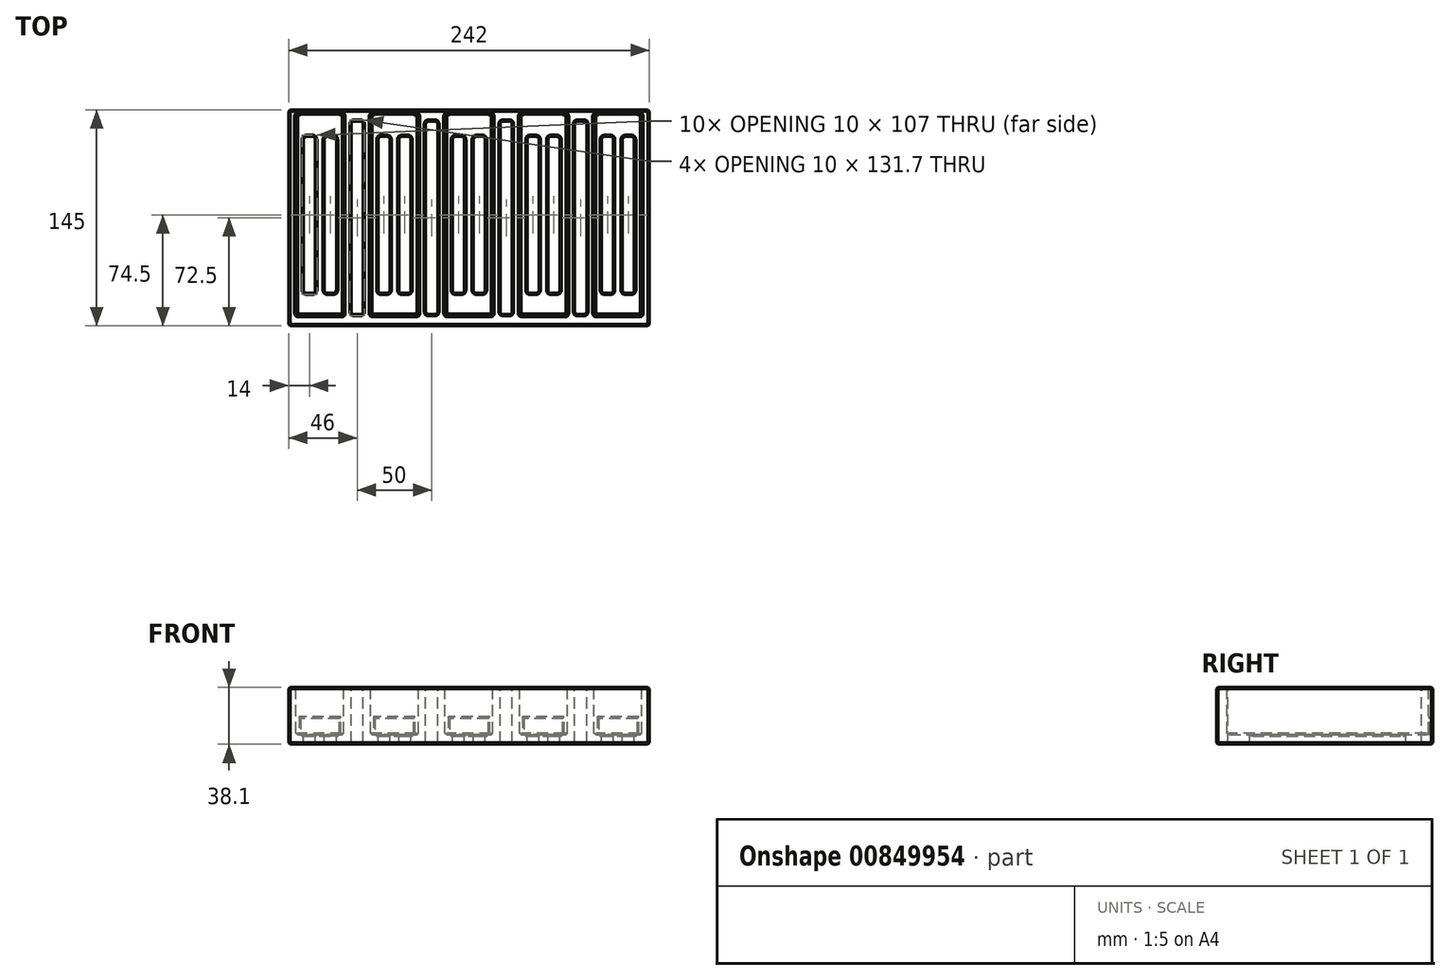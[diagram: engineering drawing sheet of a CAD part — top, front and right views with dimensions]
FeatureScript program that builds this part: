
annotation { "Feature Type Name" : "Feature", "Feature Type Description" : "" }
export const myFeature = defineFeature(function(context is Context, id is Id, definition is map)
    precondition{}
    {
        {
            var Q0;
            Q0=qCreatedBy(makeId("Top.planeOp"),FACE);
            var sketch = newSketch(context, id + "F0", { "sketchPlane" : qUnion([Q0])});
            skLineSegment(sketch, "E0.bottom", {"start": v(121, -72.5) * mm, "end": v(-121, -72.5) * mm});
            skLineSegment(sketch, "E0.top", {"start": v(121, 72.5) * mm, "end": v(-121, 72.5) * mm});
            skLineSegment(sketch, "E0.left", {"start": v(121, -72.5) * mm, "end": v(121, 72.5) * mm});
            skLineSegment(sketch, "E0.right", {"start": v(-121, -72.5) * mm, "end": v(-121, 72.5) * mm});
            skPoint(sketch, "E0.middle", {"position": v(0, 0) * mm});
            skSolve(sketch);
        }
        {
            var Q0;
            Q0=makeQuery(id+"F0.imprint","IMPRINT",FACE,{"disambiguationData":[TD([[makeQuery(id+"F0.imprint","IMPRINT",EDGE,{"derivedFrom":sQuery(id+"F0.wireOp",EDGE,"E0.bottom")}),-1.0]])]});
            extrude(context, id + "F1", {"entities" : qUnion([Q0]), "depth" : 38.1 * mm, "offsetDistance" : 25.4 * mm});
        }
        {
            var Q0;
            Q0=makeQuery(id+"F1.opExtrude","CAP_FACE",FACE,{"disambiguationData":[OSD([sQuery(id+"F0.wireOp",EDGE,"E0.bottom"),sQuery(id+"F0.wireOp",EDGE,"E0.top"),sQuery(id+"F0.wireOp",EDGE,"E0.left"),sQuery(id+"F0.wireOp",EDGE,"E0.right")])],"isStart":false});
            var sketch = newSketch(context, id + "F2", { "sketchPlane" : qUnion([Q0])});
            skLineSegment(sketch, "E1.bottom", {"start": v(-116, 69.5) * mm, "end": v(-84, 69.5) * mm});
            skLineSegment(sketch, "E1.top", {"start": v(-116, -65.5) * mm, "end": v(-84, -65.5) * mm});
            skLineSegment(sketch, "E1.left", {"start": v(-116, 69.5) * mm, "end": v(-116, -65.5) * mm});
            skLineSegment(sketch, "E1.right", {"start": v(-84, 69.5) * mm, "end": v(-84, -65.5) * mm});
            skLineSegment(sketch, "E2.1.0.0", {"start": v(-34, 69.5) * mm, "end": v(-34, -65.5) * mm});
            skLineSegment(sketch, "E2.1.0.1", {"start": v(-66, 69.5) * mm, "end": v(-34, 69.5) * mm});
            skLineSegment(sketch, "E2.1.0.2", {"start": v(-66, 69.5) * mm, "end": v(-66, -65.5) * mm});
            skLineSegment(sketch, "E2.1.0.3", {"start": v(-66, -65.5) * mm, "end": v(-34, -65.5) * mm});
            skLineSegment(sketch, "E2.2.0.0", {"start": v(16, 69.5) * mm, "end": v(16, -65.5) * mm});
            skLineSegment(sketch, "E2.2.0.1", {"start": v(-16, 69.5) * mm, "end": v(16, 69.5) * mm});
            skLineSegment(sketch, "E2.2.0.2", {"start": v(-16, 69.5) * mm, "end": v(-16, -65.5) * mm});
            skLineSegment(sketch, "E2.2.0.3", {"start": v(-16, -65.5) * mm, "end": v(16, -65.5) * mm});
            skLineSegment(sketch, "E2.direction1", {"start": v(-116, -65.5) * mm, "end": v(-66, -65.5) * mm, "construction": true});
            skLineSegment(sketch, "E3.0.3.0", {"start": v(66, 69.5) * mm, "end": v(66, -65.5) * mm});
            skLineSegment(sketch, "E3.3.3.0", {"start": v(34, 69.5) * mm, "end": v(66, 69.5) * mm});
            skLineSegment(sketch, "E3.6.3.0", {"start": v(34, 69.5) * mm, "end": v(34, -65.5) * mm});
            skLineSegment(sketch, "E3.9.3.0", {"start": v(34, -65.5) * mm, "end": v(66, -65.5) * mm});
            skLineSegment(sketch, "E3.0.4.0", {"start": v(116, 69.5) * mm, "end": v(116, -65.5) * mm});
            skLineSegment(sketch, "E3.3.4.0", {"start": v(84, 69.5) * mm, "end": v(116, 69.5) * mm});
            skLineSegment(sketch, "E3.6.4.0", {"start": v(84, 69.5) * mm, "end": v(84, -65.5) * mm});
            skLineSegment(sketch, "E3.9.4.0", {"start": v(84, -65.5) * mm, "end": v(116, -65.5) * mm});
            skSolve(sketch);
        }
        {
            var Q0;
            Q0 = qSketchRegion(id + "F2", true);
            extrude(context, id + "F3", {"entities" : qUnion([Q0]), "operationType" : NewBodyOperationType.REMOVE, "oppositeDirection" : true, "depth" : 31.75 * mm, "offsetDistance" : 25.4 * mm});
        }
        {
            var Q0;
            Q0=makeQuery(id+"F1.opExtrude","SWEPT_FACE",FACE,{"disambiguationData":[OSD([sQuery(id+"F0.wireOp",EDGE,"E0.top")])]});
            var sketch = newSketch(context, id + "F4", { "sketchPlane" : qUnion([Q0])});
            skLineSegment(sketch, "E4.top", {"start": v(87, 6.35) * mm, "end": v(113, 6.35) * mm});
            skLineSegment(sketch, "E4.left", {"start": v(87, 17.35) * mm, "end": v(87, 6.35) * mm});
            skLineSegment(sketch, "E4.right", {"start": v(113, 17.35) * mm, "end": v(113, 6.35) * mm});
            skLineSegment(sketch, "E5.1.0.1", {"start": v(37, 17.35) * mm, "end": v(37, 6.35) * mm});
            skLineSegment(sketch, "E5.1.0.2", {"start": v(37, 6.35) * mm, "end": v(63, 6.35) * mm});
            skLineSegment(sketch, "E5.1.0.3", {"start": v(63, 17.35) * mm, "end": v(63, 6.35) * mm});
            skLineSegment(sketch, "E5.2.0.1", {"start": v(-13, 17.35) * mm, "end": v(-13, 6.35) * mm});
            skLineSegment(sketch, "E5.2.0.2", {"start": v(-13, 6.35) * mm, "end": v(13, 6.35) * mm});
            skLineSegment(sketch, "E5.2.0.3", {"start": v(13, 17.35) * mm, "end": v(13, 6.35) * mm});
            skLineSegment(sketch, "E5.3.0.1", {"start": v(-63, 17.35) * mm, "end": v(-63, 6.35) * mm});
            skLineSegment(sketch, "E5.3.0.2", {"start": v(-63, 6.35) * mm, "end": v(-37, 6.35) * mm});
            skLineSegment(sketch, "E5.3.0.3", {"start": v(-37, 17.35) * mm, "end": v(-37, 6.35) * mm});
            skLineSegment(sketch, "E5.4.0.1", {"start": v(-113, 17.35) * mm, "end": v(-113, 6.35) * mm});
            skLineSegment(sketch, "E5.4.0.2", {"start": v(-113, 6.35) * mm, "end": v(-87, 6.35) * mm});
            skLineSegment(sketch, "E5.4.0.3", {"start": v(-87, 17.35) * mm, "end": v(-87, 6.35) * mm});
            skLineSegment(sketch, "E5.direction1", {"start": v(87, 17.35) * mm, "end": v(37, 17.35) * mm, "construction": true});
            skLineSegment(sketch, "E6", {"start": v(87, 17.35) * mm, "end": v(113, 17.35) * mm});
            skLineSegment(sketch, "E7.1.0.0", {"start": v(37, 17.35) * mm, "end": v(63, 17.35) * mm});
            skLineSegment(sketch, "E7.2.0.0", {"start": v(-13, 17.35) * mm, "end": v(13, 17.35) * mm});
            skLineSegment(sketch, "E7.3.0.0", {"start": v(-63, 17.35) * mm, "end": v(-37, 17.35) * mm});
            skLineSegment(sketch, "E7.4.0.0", {"start": v(-113, 17.35) * mm, "end": v(-87, 17.35) * mm});
            skSolve(sketch);
        }
        {
            var Q0;
            Q0=makeQuery(id+"F4.imprint","IMPRINT",FACE,{"disambiguationData":[TD([[makeQuery(id+"F4.imprint","IMPRINT",EDGE,{"derivedFrom":sQuery(id+"F4.wireOp",EDGE,"E4.top")}),1.0]])]});
            var Q1;
            Q1=makeQuery(id+"F4.imprint","IMPRINT",FACE,{"disambiguationData":[TD([[makeQuery(id+"F4.imprint","IMPRINT",EDGE,{"derivedFrom":sQuery(id+"F4.wireOp",EDGE,"E5.1.0.1")}),1.0]])]});
            var Q2;
            Q2=makeQuery(id+"F4.imprint","IMPRINT",FACE,{"disambiguationData":[TD([[makeQuery(id+"F4.imprint","IMPRINT",EDGE,{"derivedFrom":sQuery(id+"F4.wireOp",EDGE,"E5.2.0.1")}),1.0]])]});
            var Q3;
            Q3=makeQuery(id+"F4.imprint","IMPRINT",FACE,{"disambiguationData":[TD([[makeQuery(id+"F4.imprint","IMPRINT",EDGE,{"derivedFrom":sQuery(id+"F4.wireOp",EDGE,"E5.3.0.1")}),1.0]])]});
            var Q4;
            Q4=makeQuery(id+"F4.imprint","IMPRINT",FACE,{"disambiguationData":[TD([[makeQuery(id+"F4.imprint","IMPRINT",EDGE,{"derivedFrom":sQuery(id+"F4.wireOp",EDGE,"E5.4.0.1")}),1.0]])]});
            extrude(context, id + "F5", {"entities" : qUnion([Q0, Q1, Q2, Q3, Q4]), "operationType" : NewBodyOperationType.REMOVE, "endBound" : BoundingType.UP_TO_NEXT, "oppositeDirection" : true, "depth" : 25.4 * mm, "offsetDistance" : 25.4 * mm});
        }
        {
            var Q0;
            Q0=makeQuery(id+"F1.opExtrude","CAP_FACE",FACE,{"disambiguationData":[OSD([sQuery(id+"F0.wireOp",EDGE,"E0.bottom"),sQuery(id+"F0.wireOp",EDGE,"E0.top"),sQuery(id+"F0.wireOp",EDGE,"E0.left"),sQuery(id+"F0.wireOp",EDGE,"E0.right")])],"isStart":false});
            var sketch = newSketch(context, id + "F6", { "sketchPlane" : qUnion([Q0])});
            skLineSegment(sketch, "E8.bottom", {"start": v(-77, 64.85) * mm, "end": v(-73, 64.85) * mm});
            skLineSegment(sketch, "E8.top", {"start": v(-77, -64.85) * mm, "end": v(-73, -64.85) * mm});
            skLineSegment(sketch, "E8.left", {"start": v(-79, 62.85) * mm, "end": v(-79, -62.85) * mm});
            skLineSegment(sketch, "E8.right", {"start": v(-71, 62.85) * mm, "end": v(-71, -62.85) * mm});
            skPoint(sketch, "E9.visualSharp", {"position": v(-79, 64.85) * mm});
            skArc(sketch, "E9.filletArc", {"start": v(-77, 64.85) * mm, "mid": v(-78.41, 64.26) * mm, "end": v(-79, 62.85) * mm});
            skPoint(sketch, "E10.visualSharp", {"position": v(-71, 64.85) * mm});
            skArc(sketch, "E10.filletArc", {"start": v(-71, 62.85) * mm, "mid": v(-71.59, 64.26) * mm, "end": v(-73, 64.85) * mm});
            skPoint(sketch, "E11.visualSharp", {"position": v(-79, -64.85) * mm});
            skArc(sketch, "E11.filletArc", {"start": v(-79, -62.85) * mm, "mid": v(-78.41, -64.26) * mm, "end": v(-77, -64.85) * mm});
            skPoint(sketch, "E12.visualSharp", {"position": v(-71, -64.85) * mm});
            skArc(sketch, "E12.filletArc", {"start": v(-73, -64.85) * mm, "mid": v(-71.59, -64.26) * mm, "end": v(-71, -62.85) * mm});
            skLineSegment(sketch, "E13.1.0.0", {"start": v(-29, 62.85) * mm, "end": v(-29, -62.85) * mm});
            skLineSegment(sketch, "E13.1.0.1", {"start": v(-21, 62.85) * mm, "end": v(-21, -62.85) * mm});
            skArc(sketch, "E13.1.0.2", {"start": v(-29, -62.85) * mm, "mid": v(-28.41, -64.26) * mm, "end": v(-27, -64.85) * mm});
            skLineSegment(sketch, "E13.1.0.3", {"start": v(-27, -64.85) * mm, "end": v(-23, -64.85) * mm});
            skArc(sketch, "E13.1.0.4", {"start": v(-23, -64.85) * mm, "mid": v(-21.59, -64.26) * mm, "end": v(-21, -62.85) * mm});
            skArc(sketch, "E13.1.0.5", {"start": v(-27, 64.85) * mm, "mid": v(-28.41, 64.26) * mm, "end": v(-29, 62.85) * mm});
            skLineSegment(sketch, "E13.1.0.6", {"start": v(-27, 64.85) * mm, "end": v(-23, 64.85) * mm});
            skArc(sketch, "E13.1.0.7", {"start": v(-21, 62.85) * mm, "mid": v(-21.59, 64.26) * mm, "end": v(-23, 64.85) * mm});
            skLineSegment(sketch, "E13.2.0.0", {"start": v(21, 62.85) * mm, "end": v(21, -62.85) * mm});
            skLineSegment(sketch, "E13.2.0.1", {"start": v(29, 62.85) * mm, "end": v(29, -62.85) * mm});
            skArc(sketch, "E13.2.0.2", {"start": v(21, -62.85) * mm, "mid": v(21.59, -64.26) * mm, "end": v(23, -64.85) * mm});
            skLineSegment(sketch, "E13.2.0.3", {"start": v(23, -64.85) * mm, "end": v(27, -64.85) * mm});
            skArc(sketch, "E13.2.0.4", {"start": v(27, -64.85) * mm, "mid": v(28.41, -64.26) * mm, "end": v(29, -62.85) * mm});
            skArc(sketch, "E13.2.0.5", {"start": v(23, 64.85) * mm, "mid": v(21.59, 64.26) * mm, "end": v(21, 62.85) * mm});
            skLineSegment(sketch, "E13.2.0.6", {"start": v(23, 64.85) * mm, "end": v(27, 64.85) * mm});
            skArc(sketch, "E13.2.0.7", {"start": v(29, 62.85) * mm, "mid": v(28.41, 64.26) * mm, "end": v(27, 64.85) * mm});
            skLineSegment(sketch, "E13.3.0.0", {"start": v(71, 62.85) * mm, "end": v(71, -62.85) * mm});
            skLineSegment(sketch, "E13.3.0.1", {"start": v(79, 62.85) * mm, "end": v(79, -62.85) * mm});
            skArc(sketch, "E13.3.0.2", {"start": v(71, -62.85) * mm, "mid": v(71.59, -64.26) * mm, "end": v(73, -64.85) * mm});
            skLineSegment(sketch, "E13.3.0.3", {"start": v(73, -64.85) * mm, "end": v(77, -64.85) * mm});
            skArc(sketch, "E13.3.0.4", {"start": v(77, -64.85) * mm, "mid": v(78.41, -64.26) * mm, "end": v(79, -62.85) * mm});
            skArc(sketch, "E13.3.0.5", {"start": v(73, 64.85) * mm, "mid": v(71.59, 64.26) * mm, "end": v(71, 62.85) * mm});
            skLineSegment(sketch, "E13.3.0.6", {"start": v(73, 64.85) * mm, "end": v(77, 64.85) * mm});
            skArc(sketch, "E13.3.0.7", {"start": v(79, 62.85) * mm, "mid": v(78.41, 64.26) * mm, "end": v(77, 64.85) * mm});
            skLineSegment(sketch, "E13.direction1", {"start": v(-79, -62.85) * mm, "end": v(-29, -62.85) * mm, "construction": true});
            skSolve(sketch);
        }
        {
            var Q0;
            Q0=makeQuery(id+"F6.imprint","IMPRINT",FACE,{"disambiguationData":[TD([[makeQuery(id+"F6.imprint","IMPRINT",EDGE,{"derivedFrom":sQuery(id+"F6.wireOp",EDGE,"E8.bottom")}),-1.0]])]});
            var Q1;
            Q1=makeQuery(id+"F6.imprint","IMPRINT",FACE,{"disambiguationData":[TD([[makeQuery(id+"F6.imprint","IMPRINT",EDGE,{"derivedFrom":sQuery(id+"F6.wireOp",EDGE,"E13.2.0.0")}),1.0]])]});
            var Q2;
            Q2=makeQuery(id+"F6.imprint","IMPRINT",FACE,{"disambiguationData":[TD([[makeQuery(id+"F6.imprint","IMPRINT",EDGE,{"derivedFrom":sQuery(id+"F6.wireOp",EDGE,"E13.3.0.0")}),1.0]])]});
            var Q3;
            Q3=makeQuery(id+"F6.imprint","IMPRINT",FACE,{"disambiguationData":[TD([[makeQuery(id+"F6.imprint","IMPRINT",EDGE,{"derivedFrom":sQuery(id+"F6.wireOp",EDGE,"E13.1.0.0")}),1.0]])]});
            extrude(context, id + "F7", {"entities" : qUnion([Q0, Q1, Q2, Q3]), "operationType" : NewBodyOperationType.REMOVE, "endBound" : BoundingType.THROUGH_ALL, "oppositeDirection" : true, "depth" : 25 * mm, "offsetDistance" : 25 * mm});
        }
        {
            var Q0;
            Q0=makeQuery(id+"F3.boolean.opBoolean","COPY",EDGE,{"derivedFrom":makeQuery(id+"F3.opExtrude","SWEPT_EDGE",EDGE,{"disambiguationData":[OSD([sQuery(id+"F2.wireOp",EDGE,"E1.bottom"),sQuery(id+"F2.wireOp",EDGE,"E1.left")])]})});
            var Q1;
            Q1=makeQuery(id+"F3.boolean.opBoolean","COPY",EDGE,{"derivedFrom":makeQuery(id+"F3.opExtrude","SWEPT_EDGE",EDGE,{"disambiguationData":[OSD([sQuery(id+"F2.wireOp",EDGE,"E1.bottom"),sQuery(id+"F2.wireOp",EDGE,"E1.right")])]})});
            var Q2;
            Q2=makeQuery(id+"F3.boolean.opBoolean","COPY",EDGE,{"derivedFrom":makeQuery(id+"F3.opExtrude","SWEPT_EDGE",EDGE,{"disambiguationData":[OSD([sQuery(id+"F2.wireOp",EDGE,"E1.top"),sQuery(id+"F2.wireOp",EDGE,"E1.left")])]})});
            var Q3;
            Q3=makeQuery(id+"F3.boolean.opBoolean","COPY",EDGE,{"derivedFrom":makeQuery(id+"F3.opExtrude","SWEPT_EDGE",EDGE,{"disambiguationData":[OSD([sQuery(id+"F2.wireOp",EDGE,"E1.top"),sQuery(id+"F2.wireOp",EDGE,"E1.right")])]})});
            var Q4;
            Q4=makeQuery(id+"F3.boolean.opBoolean","COPY",EDGE,{"derivedFrom":makeQuery(id+"F3.opExtrude","SWEPT_EDGE",EDGE,{"disambiguationData":[OSD([sQuery(id+"F2.wireOp",EDGE,"E2.1.0.2"),sQuery(id+"F2.wireOp",EDGE,"E2.1.0.3")])]})});
            var Q5;
            Q5=makeQuery(id+"F3.boolean.opBoolean","COPY",EDGE,{"derivedFrom":makeQuery(id+"F3.opExtrude","SWEPT_EDGE",EDGE,{"disambiguationData":[OSD([sQuery(id+"F2.wireOp",EDGE,"E2.1.0.1"),sQuery(id+"F2.wireOp",EDGE,"E2.1.0.2")])]})});
            var Q6;
            Q6=makeQuery(id+"F3.boolean.opBoolean","COPY",EDGE,{"derivedFrom":makeQuery(id+"F3.opExtrude","SWEPT_EDGE",EDGE,{"disambiguationData":[OSD([sQuery(id+"F2.wireOp",EDGE,"E2.1.0.0"),sQuery(id+"F2.wireOp",EDGE,"E2.1.0.1")])]})});
            var Q7;
            Q7=makeQuery(id+"F3.boolean.opBoolean","COPY",EDGE,{"derivedFrom":makeQuery(id+"F3.opExtrude","SWEPT_EDGE",EDGE,{"disambiguationData":[OSD([sQuery(id+"F2.wireOp",EDGE,"E2.1.0.0"),sQuery(id+"F2.wireOp",EDGE,"E2.1.0.3")])]})});
            var Q8;
            Q8=makeQuery(id+"F3.boolean.opBoolean","COPY",EDGE,{"derivedFrom":makeQuery(id+"F3.opExtrude","SWEPT_EDGE",EDGE,{"disambiguationData":[OSD([sQuery(id+"F2.wireOp",EDGE,"E2.2.0.1"),sQuery(id+"F2.wireOp",EDGE,"E2.2.0.2")])]})});
            var Q9;
            Q9=makeQuery(id+"F3.boolean.opBoolean","COPY",EDGE,{"derivedFrom":makeQuery(id+"F3.opExtrude","SWEPT_EDGE",EDGE,{"disambiguationData":[OSD([sQuery(id+"F2.wireOp",EDGE,"E2.2.0.0"),sQuery(id+"F2.wireOp",EDGE,"E2.2.0.1")])]})});
            var Q10;
            Q10=makeQuery(id+"F3.boolean.opBoolean","COPY",EDGE,{"derivedFrom":makeQuery(id+"F3.opExtrude","SWEPT_EDGE",EDGE,{"disambiguationData":[OSD([sQuery(id+"F2.wireOp",EDGE,"E2.2.0.2"),sQuery(id+"F2.wireOp",EDGE,"E2.2.0.3")])]})});
            var Q11;
            Q11=makeQuery(id+"F3.boolean.opBoolean","COPY",EDGE,{"derivedFrom":makeQuery(id+"F3.opExtrude","SWEPT_EDGE",EDGE,{"disambiguationData":[OSD([sQuery(id+"F2.wireOp",EDGE,"E2.2.0.0"),sQuery(id+"F2.wireOp",EDGE,"E2.2.0.3")])]})});
            var Q12;
            Q12=makeQuery(id+"F3.boolean.opBoolean","COPY",EDGE,{"derivedFrom":makeQuery(id+"F3.opExtrude","SWEPT_EDGE",EDGE,{"disambiguationData":[OSD([sQuery(id+"F2.wireOp",EDGE,"E3.3.3.0"),sQuery(id+"F2.wireOp",EDGE,"E3.6.3.0")])]})});
            var Q13;
            Q13=makeQuery(id+"F3.boolean.opBoolean","COPY",EDGE,{"derivedFrom":makeQuery(id+"F3.opExtrude","SWEPT_EDGE",EDGE,{"disambiguationData":[OSD([sQuery(id+"F2.wireOp",EDGE,"E3.6.3.0"),sQuery(id+"F2.wireOp",EDGE,"E3.9.3.0")])]})});
            var Q14;
            Q14=makeQuery(id+"F3.boolean.opBoolean","COPY",EDGE,{"derivedFrom":makeQuery(id+"F3.opExtrude","SWEPT_EDGE",EDGE,{"disambiguationData":[OSD([sQuery(id+"F2.wireOp",EDGE,"E3.0.3.0"),sQuery(id+"F2.wireOp",EDGE,"E3.9.3.0")])]})});
            var Q15;
            Q15=makeQuery(id+"F3.boolean.opBoolean","COPY",EDGE,{"derivedFrom":makeQuery(id+"F3.opExtrude","SWEPT_EDGE",EDGE,{"disambiguationData":[OSD([sQuery(id+"F2.wireOp",EDGE,"E3.0.3.0"),sQuery(id+"F2.wireOp",EDGE,"E3.3.3.0")])]})});
            var Q16;
            Q16=makeQuery(id+"F3.boolean.opBoolean","COPY",EDGE,{"derivedFrom":makeQuery(id+"F3.opExtrude","SWEPT_EDGE",EDGE,{"disambiguationData":[OSD([sQuery(id+"F2.wireOp",EDGE,"E3.3.4.0"),sQuery(id+"F2.wireOp",EDGE,"E3.6.4.0")])]})});
            var Q17;
            Q17=makeQuery(id+"F3.boolean.opBoolean","COPY",EDGE,{"derivedFrom":makeQuery(id+"F3.opExtrude","SWEPT_EDGE",EDGE,{"disambiguationData":[OSD([sQuery(id+"F2.wireOp",EDGE,"E3.0.4.0"),sQuery(id+"F2.wireOp",EDGE,"E3.3.4.0")])]})});
            var Q18;
            Q18=makeQuery(id+"F3.boolean.opBoolean","COPY",EDGE,{"derivedFrom":makeQuery(id+"F3.opExtrude","SWEPT_EDGE",EDGE,{"disambiguationData":[OSD([sQuery(id+"F2.wireOp",EDGE,"E3.6.4.0"),sQuery(id+"F2.wireOp",EDGE,"E3.9.4.0")])]})});
            var Q19;
            Q19=makeQuery(id+"F3.boolean.opBoolean","COPY",EDGE,{"derivedFrom":makeQuery(id+"F3.opExtrude","SWEPT_EDGE",EDGE,{"disambiguationData":[OSD([sQuery(id+"F2.wireOp",EDGE,"E3.0.4.0"),sQuery(id+"F2.wireOp",EDGE,"E3.9.4.0")])]})});
            fillet(context, id + "F8", {"entities" : qUnion([Q0, Q1, Q2, Q3, Q4, Q5, Q6, Q7, Q8, Q9, Q10, Q11, Q12, Q13, Q14, Q15, Q16, Q17, Q18, Q19]), "radius" : 1.5 * mm, "tangentPropagation" : true, "allowEdgeOverflow" : false});
        }
        {
            var Q0;
            Q0=makeQuery(id+"F5.boolean.opBoolean","MERGE",FACE,{"derivedFrom":[makeQuery(id+"F3.boolean.opBoolean","COPY",FACE,{"derivedFrom":makeQuery(id+"F3.opExtrude","CAP_FACE",FACE,{"disambiguationData":[OSD([sQuery(id+"F2.wireOp",EDGE,"E1.bottom"),sQuery(id+"F2.wireOp",EDGE,"E1.top"),sQuery(id+"F2.wireOp",EDGE,"E1.left"),sQuery(id+"F2.wireOp",EDGE,"E1.right")])],"isStart":false})}),makeQuery(id+"F5.opExtrude","SWEPT_FACE",FACE,{"disambiguationData":[OSD([sQuery(id+"F4.wireOp",EDGE,"E4.top")])]})]});
            var sketch = newSketch(context, id + "F9", { "sketchPlane" : qUnion([Q0])});
            skLineSegment(sketch, "E14.bottom", {"start": v(-109, 54.5) * mm, "end": v(-105, 54.5) * mm});
            skLineSegment(sketch, "E14.top", {"start": v(-109, -50.5) * mm, "end": v(-105, -50.5) * mm});
            skLineSegment(sketch, "E14.left", {"start": v(-111, 52.5) * mm, "end": v(-111, -48.5) * mm});
            skLineSegment(sketch, "E14.right", {"start": v(-103, 52.5) * mm, "end": v(-103, -48.5) * mm});
            skLineSegment(sketch, "E15.bottom", {"start": v(-95, 54.5) * mm, "end": v(-91, 54.5) * mm});
            skLineSegment(sketch, "E15.top", {"start": v(-95, -50.5) * mm, "end": v(-91, -50.5) * mm});
            skLineSegment(sketch, "E15.left", {"start": v(-97, 52.5) * mm, "end": v(-97, -48.5) * mm});
            skLineSegment(sketch, "E15.right", {"start": v(-89, 52.5) * mm, "end": v(-89, -48.5) * mm});
            skPoint(sketch, "E16.visualSharp", {"position": v(-111, 54.5) * mm});
            skArc(sketch, "E16.filletArc", {"start": v(-109, 54.5) * mm, "mid": v(-110.41, 53.91) * mm, "end": v(-111, 52.5) * mm});
            skPoint(sketch, "E17.visualSharp", {"position": v(-103, 54.5) * mm});
            skArc(sketch, "E17.filletArc", {"start": v(-103, 52.5) * mm, "mid": v(-103.59, 53.91) * mm, "end": v(-105, 54.5) * mm});
            skPoint(sketch, "E18.visualSharp", {"position": v(-111, -50.5) * mm});
            skArc(sketch, "E18.filletArc", {"start": v(-111, -48.5) * mm, "mid": v(-110.41, -49.91) * mm, "end": v(-109, -50.5) * mm});
            skPoint(sketch, "E19.visualSharp", {"position": v(-103, -50.5) * mm});
            skArc(sketch, "E19.filletArc", {"start": v(-105, -50.5) * mm, "mid": v(-103.59, -49.91) * mm, "end": v(-103, -48.5) * mm});
            skPoint(sketch, "E20.visualSharp", {"position": v(-97, 54.5) * mm});
            skArc(sketch, "E20.filletArc", {"start": v(-95, 54.5) * mm, "mid": v(-96.41, 53.91) * mm, "end": v(-97, 52.5) * mm});
            skPoint(sketch, "E21.visualSharp", {"position": v(-89, 54.5) * mm});
            skArc(sketch, "E21.filletArc", {"start": v(-89, 52.5) * mm, "mid": v(-89.59, 53.91) * mm, "end": v(-91, 54.5) * mm});
            skPoint(sketch, "E22.visualSharp", {"position": v(-89, -50.5) * mm});
            skArc(sketch, "E22.filletArc", {"start": v(-91, -50.5) * mm, "mid": v(-89.59, -49.91) * mm, "end": v(-89, -48.5) * mm});
            skPoint(sketch, "E23.visualSharp", {"position": v(-97, -50.5) * mm});
            skArc(sketch, "E23.filletArc", {"start": v(-97, -48.5) * mm, "mid": v(-96.41, -49.91) * mm, "end": v(-95, -50.5) * mm});
            skLineSegment(sketch, "E24.1.0.0", {"start": v(-47, 52.5) * mm, "end": v(-47, -48.5) * mm});
            skPoint(sketch, "E24.1.0.1", {"position": v(-61, 54.5) * mm});
            skPoint(sketch, "E24.1.0.2", {"position": v(-53, -50.5) * mm});
            skLineSegment(sketch, "E24.1.0.3", {"start": v(-53, 52.5) * mm, "end": v(-53, -48.5) * mm});
            skPoint(sketch, "E24.1.0.4", {"position": v(-61, -50.5) * mm});
            skLineSegment(sketch, "E24.1.0.5", {"start": v(-61, 52.5) * mm, "end": v(-61, -48.5) * mm});
            skPoint(sketch, "E24.1.0.6", {"position": v(-47, -50.5) * mm});
            skPoint(sketch, "E24.1.0.7", {"position": v(-39, 54.5) * mm});
            skPoint(sketch, "E24.1.0.8", {"position": v(-53, 54.5) * mm});
            skLineSegment(sketch, "E24.1.0.9", {"start": v(-39, 52.5) * mm, "end": v(-39, -48.5) * mm});
            skPoint(sketch, "E24.1.0.10", {"position": v(-39, -50.5) * mm});
            skPoint(sketch, "E24.1.0.11", {"position": v(-47, 54.5) * mm});
            skArc(sketch, "E24.1.0.12", {"start": v(-61, -48.5) * mm, "mid": v(-60.41, -49.91) * mm, "end": v(-59, -50.5) * mm});
            skArc(sketch, "E24.1.0.13", {"start": v(-47, -48.5) * mm, "mid": v(-46.41, -49.91) * mm, "end": v(-45, -50.5) * mm});
            skArc(sketch, "E24.1.0.14", {"start": v(-59, 54.5) * mm, "mid": v(-60.41, 53.91) * mm, "end": v(-61, 52.5) * mm});
            skLineSegment(sketch, "E24.1.0.15", {"start": v(-59, -50.5) * mm, "end": v(-55, -50.5) * mm});
            skLineSegment(sketch, "E24.1.0.16", {"start": v(-45, -50.5) * mm, "end": v(-41, -50.5) * mm});
            skArc(sketch, "E24.1.0.17", {"start": v(-45, 54.5) * mm, "mid": v(-46.41, 53.91) * mm, "end": v(-47, 52.5) * mm});
            skArc(sketch, "E24.1.0.18", {"start": v(-55, -50.5) * mm, "mid": v(-53.59, -49.91) * mm, "end": v(-53, -48.5) * mm});
            skArc(sketch, "E24.1.0.19", {"start": v(-41, -50.5) * mm, "mid": v(-39.59, -49.91) * mm, "end": v(-39, -48.5) * mm});
            skLineSegment(sketch, "E24.1.0.20", {"start": v(-59, 54.5) * mm, "end": v(-55, 54.5) * mm});
            skArc(sketch, "E24.1.0.21", {"start": v(-39, 52.5) * mm, "mid": v(-39.59, 53.91) * mm, "end": v(-41, 54.5) * mm});
            skArc(sketch, "E24.1.0.22", {"start": v(-53, 52.5) * mm, "mid": v(-53.59, 53.91) * mm, "end": v(-55, 54.5) * mm});
            skLineSegment(sketch, "E24.1.0.23", {"start": v(-45, 54.5) * mm, "end": v(-41, 54.5) * mm});
            skLineSegment(sketch, "E24.2.0.0", {"start": v(3, 52.5) * mm, "end": v(3, -48.5) * mm});
            skPoint(sketch, "E24.2.0.1", {"position": v(-11, 54.5) * mm});
            skPoint(sketch, "E24.2.0.2", {"position": v(-3, -50.5) * mm});
            skLineSegment(sketch, "E24.2.0.3", {"start": v(-3, 52.5) * mm, "end": v(-3, -48.5) * mm});
            skPoint(sketch, "E24.2.0.4", {"position": v(-11, -50.5) * mm});
            skLineSegment(sketch, "E24.2.0.5", {"start": v(-11, 52.5) * mm, "end": v(-11, -48.5) * mm});
            skPoint(sketch, "E24.2.0.6", {"position": v(3, -50.5) * mm});
            skPoint(sketch, "E24.2.0.7", {"position": v(11, 54.5) * mm});
            skPoint(sketch, "E24.2.0.8", {"position": v(-3, 54.5) * mm});
            skLineSegment(sketch, "E24.2.0.9", {"start": v(11, 52.5) * mm, "end": v(11, -48.5) * mm});
            skPoint(sketch, "E24.2.0.10", {"position": v(11, -50.5) * mm});
            skPoint(sketch, "E24.2.0.11", {"position": v(3, 54.5) * mm});
            skArc(sketch, "E24.2.0.12", {"start": v(-11, -48.5) * mm, "mid": v(-10.41, -49.91) * mm, "end": v(-9, -50.5) * mm});
            skArc(sketch, "E24.2.0.13", {"start": v(3, -48.5) * mm, "mid": v(3.59, -49.91) * mm, "end": v(5, -50.5) * mm});
            skArc(sketch, "E24.2.0.14", {"start": v(-9, 54.5) * mm, "mid": v(-10.41, 53.91) * mm, "end": v(-11, 52.5) * mm});
            skLineSegment(sketch, "E24.2.0.15", {"start": v(-9, -50.5) * mm, "end": v(-5, -50.5) * mm});
            skLineSegment(sketch, "E24.2.0.16", {"start": v(5, -50.5) * mm, "end": v(9, -50.5) * mm});
            skArc(sketch, "E24.2.0.17", {"start": v(5, 54.5) * mm, "mid": v(3.59, 53.91) * mm, "end": v(3, 52.5) * mm});
            skArc(sketch, "E24.2.0.18", {"start": v(-5, -50.5) * mm, "mid": v(-3.59, -49.91) * mm, "end": v(-3, -48.5) * mm});
            skArc(sketch, "E24.2.0.19", {"start": v(9, -50.5) * mm, "mid": v(10.41, -49.91) * mm, "end": v(11, -48.5) * mm});
            skLineSegment(sketch, "E24.2.0.20", {"start": v(-9, 54.5) * mm, "end": v(-5, 54.5) * mm});
            skArc(sketch, "E24.2.0.21", {"start": v(11, 52.5) * mm, "mid": v(10.41, 53.91) * mm, "end": v(9, 54.5) * mm});
            skArc(sketch, "E24.2.0.22", {"start": v(-3, 52.5) * mm, "mid": v(-3.59, 53.91) * mm, "end": v(-5, 54.5) * mm});
            skLineSegment(sketch, "E24.2.0.23", {"start": v(5, 54.5) * mm, "end": v(9, 54.5) * mm});
            skLineSegment(sketch, "E24.3.0.0", {"start": v(53, 52.5) * mm, "end": v(53, -48.5) * mm});
            skPoint(sketch, "E24.3.0.1", {"position": v(39, 54.5) * mm});
            skPoint(sketch, "E24.3.0.2", {"position": v(47, -50.5) * mm});
            skLineSegment(sketch, "E24.3.0.3", {"start": v(47, 52.5) * mm, "end": v(47, -48.5) * mm});
            skPoint(sketch, "E24.3.0.4", {"position": v(39, -50.5) * mm});
            skLineSegment(sketch, "E24.3.0.5", {"start": v(39, 52.5) * mm, "end": v(39, -48.5) * mm});
            skPoint(sketch, "E24.3.0.6", {"position": v(53, -50.5) * mm});
            skPoint(sketch, "E24.3.0.7", {"position": v(61, 54.5) * mm});
            skPoint(sketch, "E24.3.0.8", {"position": v(47, 54.5) * mm});
            skLineSegment(sketch, "E24.3.0.9", {"start": v(61, 52.5) * mm, "end": v(61, -48.5) * mm});
            skPoint(sketch, "E24.3.0.10", {"position": v(61, -50.5) * mm});
            skPoint(sketch, "E24.3.0.11", {"position": v(53, 54.5) * mm});
            skArc(sketch, "E24.3.0.12", {"start": v(39, -48.5) * mm, "mid": v(39.59, -49.91) * mm, "end": v(41, -50.5) * mm});
            skArc(sketch, "E24.3.0.13", {"start": v(53, -48.5) * mm, "mid": v(53.59, -49.91) * mm, "end": v(55, -50.5) * mm});
            skArc(sketch, "E24.3.0.14", {"start": v(41, 54.5) * mm, "mid": v(39.59, 53.91) * mm, "end": v(39, 52.5) * mm});
            skLineSegment(sketch, "E24.3.0.15", {"start": v(41, -50.5) * mm, "end": v(45, -50.5) * mm});
            skLineSegment(sketch, "E24.3.0.16", {"start": v(55, -50.5) * mm, "end": v(59, -50.5) * mm});
            skArc(sketch, "E24.3.0.17", {"start": v(55, 54.5) * mm, "mid": v(53.59, 53.91) * mm, "end": v(53, 52.5) * mm});
            skArc(sketch, "E24.3.0.18", {"start": v(45, -50.5) * mm, "mid": v(46.41, -49.91) * mm, "end": v(47, -48.5) * mm});
            skArc(sketch, "E24.3.0.19", {"start": v(59, -50.5) * mm, "mid": v(60.41, -49.91) * mm, "end": v(61, -48.5) * mm});
            skLineSegment(sketch, "E24.3.0.20", {"start": v(41, 54.5) * mm, "end": v(45, 54.5) * mm});
            skArc(sketch, "E24.3.0.21", {"start": v(61, 52.5) * mm, "mid": v(60.41, 53.91) * mm, "end": v(59, 54.5) * mm});
            skArc(sketch, "E24.3.0.22", {"start": v(47, 52.5) * mm, "mid": v(46.41, 53.91) * mm, "end": v(45, 54.5) * mm});
            skLineSegment(sketch, "E24.3.0.23", {"start": v(55, 54.5) * mm, "end": v(59, 54.5) * mm});
            skLineSegment(sketch, "E24.4.0.0", {"start": v(103, 52.5) * mm, "end": v(103, -48.5) * mm});
            skPoint(sketch, "E24.4.0.1", {"position": v(89, 54.5) * mm});
            skPoint(sketch, "E24.4.0.2", {"position": v(97, -50.5) * mm});
            skLineSegment(sketch, "E24.4.0.3", {"start": v(97, 52.5) * mm, "end": v(97, -48.5) * mm});
            skPoint(sketch, "E24.4.0.4", {"position": v(89, -50.5) * mm});
            skLineSegment(sketch, "E24.4.0.5", {"start": v(89, 52.5) * mm, "end": v(89, -48.5) * mm});
            skPoint(sketch, "E24.4.0.6", {"position": v(103, -50.5) * mm});
            skPoint(sketch, "E24.4.0.7", {"position": v(111, 54.5) * mm});
            skPoint(sketch, "E24.4.0.8", {"position": v(97, 54.5) * mm});
            skLineSegment(sketch, "E24.4.0.9", {"start": v(111, 52.5) * mm, "end": v(111, -48.5) * mm});
            skPoint(sketch, "E24.4.0.10", {"position": v(111, -50.5) * mm});
            skPoint(sketch, "E24.4.0.11", {"position": v(103, 54.5) * mm});
            skArc(sketch, "E24.4.0.12", {"start": v(89, -48.5) * mm, "mid": v(89.59, -49.91) * mm, "end": v(91, -50.5) * mm});
            skArc(sketch, "E24.4.0.13", {"start": v(103, -48.5) * mm, "mid": v(103.59, -49.91) * mm, "end": v(105, -50.5) * mm});
            skArc(sketch, "E24.4.0.14", {"start": v(91, 54.5) * mm, "mid": v(89.59, 53.91) * mm, "end": v(89, 52.5) * mm});
            skLineSegment(sketch, "E24.4.0.15", {"start": v(91, -50.5) * mm, "end": v(95, -50.5) * mm});
            skLineSegment(sketch, "E24.4.0.16", {"start": v(105, -50.5) * mm, "end": v(109, -50.5) * mm});
            skArc(sketch, "E24.4.0.17", {"start": v(105, 54.5) * mm, "mid": v(103.59, 53.91) * mm, "end": v(103, 52.5) * mm});
            skArc(sketch, "E24.4.0.18", {"start": v(95, -50.5) * mm, "mid": v(96.41, -49.91) * mm, "end": v(97, -48.5) * mm});
            skArc(sketch, "E24.4.0.19", {"start": v(109, -50.5) * mm, "mid": v(110.41, -49.91) * mm, "end": v(111, -48.5) * mm});
            skLineSegment(sketch, "E24.4.0.20", {"start": v(91, 54.5) * mm, "end": v(95, 54.5) * mm});
            skArc(sketch, "E24.4.0.21", {"start": v(111, 52.5) * mm, "mid": v(110.41, 53.91) * mm, "end": v(109, 54.5) * mm});
            skArc(sketch, "E24.4.0.22", {"start": v(97, 52.5) * mm, "mid": v(96.41, 53.91) * mm, "end": v(95, 54.5) * mm});
            skLineSegment(sketch, "E24.4.0.23", {"start": v(105, 54.5) * mm, "end": v(109, 54.5) * mm});
            skLineSegment(sketch, "E24.direction1", {"start": v(-111, -50.5) * mm, "end": v(-61, -50.5) * mm, "construction": true});
            skSolve(sketch);
        }
        {
            var Q0;
            Q0 = qSketchRegion(id + "F9", true);
            extrude(context, id + "F10", {"entities" : qUnion([Q0]), "operationType" : NewBodyOperationType.REMOVE, "endBound" : BoundingType.THROUGH_ALL, "oppositeDirection" : true, "depth" : 25 * mm, "offsetDistance" : 25 * mm});
        }
        {
            var Q0;
            Q0=makeQuery(id+"F3.boolean.opBoolean","COPY",EDGE,{"derivedFrom":makeQuery(id+"F3.opExtrude","CAP_EDGE",EDGE,{"disambiguationData":[OSD([sQuery(id+"F2.wireOp",EDGE,"E1.bottom")])],"isStart":true})});
            var Q1;
            Q1=makeQuery(id+"F3.boolean.opBoolean","COPY",EDGE,{"derivedFrom":makeQuery(id+"F3.opExtrude","CAP_EDGE",EDGE,{"disambiguationData":[OSD([sQuery(id+"F2.wireOp",EDGE,"E1.right")])],"isStart":true})});
            var Q2;
            Q2=makeQuery(id+"F3.boolean.opBoolean","COPY",EDGE,{"derivedFrom":makeQuery(id+"F3.opExtrude","CAP_EDGE",EDGE,{"disambiguationData":[OSD([sQuery(id+"F2.wireOp",EDGE,"E1.left")])],"isStart":true})});
            var Q3;
            Q3=makeQuery(id+"F3.boolean.opBoolean","COPY",EDGE,{"derivedFrom":makeQuery(id+"F3.opExtrude","CAP_EDGE",EDGE,{"disambiguationData":[OSD([sQuery(id+"F2.wireOp",EDGE,"E1.top")])],"isStart":true})});
            var Q4;
            Q4=makeQuery(id+"F1.opExtrude","CAP_FACE",FACE,{"disambiguationData":[OSD([sQuery(id+"F0.wireOp",EDGE,"E0.bottom"),sQuery(id+"F0.wireOp",EDGE,"E0.top"),sQuery(id+"F0.wireOp",EDGE,"E0.left"),sQuery(id+"F0.wireOp",EDGE,"E0.right")])],"isStart":false});
            var Q5;
            Q5=makeQuery(id+"F1.opExtrude","SWEPT_FACE",FACE,{"disambiguationData":[OSD([sQuery(id+"F0.wireOp",EDGE,"E0.bottom")])]});
            var Q6;
            Q6=makeQuery(id+"F1.opExtrude","SWEPT_FACE",FACE,{"disambiguationData":[OSD([sQuery(id+"F0.wireOp",EDGE,"E0.top")])]});
            var Q7;
            Q7=makeQuery(id+"F1.opExtrude","SWEPT_FACE",FACE,{"disambiguationData":[OSD([sQuery(id+"F0.wireOp",EDGE,"E0.left")])]});
            var Q8;
            Q8=makeQuery(id+"F1.opExtrude","CAP_FACE",FACE,{"disambiguationData":[OSD([sQuery(id+"F0.wireOp",EDGE,"E0.bottom"),sQuery(id+"F0.wireOp",EDGE,"E0.top"),sQuery(id+"F0.wireOp",EDGE,"E0.left"),sQuery(id+"F0.wireOp",EDGE,"E0.right")])],"isStart":true});
            var Q9;
            Q9=makeQuery(id+"F5.boolean.opBoolean","MERGE",FACE,{"derivedFrom":[makeQuery(id+"F3.boolean.opBoolean","COPY",FACE,{"derivedFrom":makeQuery(id+"F3.opExtrude","CAP_FACE",FACE,{"disambiguationData":[OSD([sQuery(id+"F2.wireOp",EDGE,"E1.bottom"),sQuery(id+"F2.wireOp",EDGE,"E1.top"),sQuery(id+"F2.wireOp",EDGE,"E1.left"),sQuery(id+"F2.wireOp",EDGE,"E1.right")])],"isStart":false})}),makeQuery(id+"F5.opExtrude","SWEPT_FACE",FACE,{"disambiguationData":[OSD([sQuery(id+"F4.wireOp",EDGE,"E4.top")])]})]});
            var Q10;
            Q10=makeQuery(id+"F5.boolean.opBoolean","MERGE",FACE,{"derivedFrom":[makeQuery(id+"F3.boolean.opBoolean","COPY",FACE,{"derivedFrom":makeQuery(id+"F3.opExtrude","CAP_FACE",FACE,{"disambiguationData":[OSD([sQuery(id+"F2.wireOp",EDGE,"E2.1.0.0"),sQuery(id+"F2.wireOp",EDGE,"E2.1.0.1"),sQuery(id+"F2.wireOp",EDGE,"E2.1.0.2"),sQuery(id+"F2.wireOp",EDGE,"E2.1.0.3")])],"isStart":false})}),makeQuery(id+"F5.opExtrude","SWEPT_FACE",FACE,{"disambiguationData":[OSD([sQuery(id+"F4.wireOp",EDGE,"E5.1.0.2")])]})]});
            var Q11;
            Q11=makeQuery(id+"F5.boolean.opBoolean","MERGE",FACE,{"derivedFrom":[makeQuery(id+"F3.boolean.opBoolean","COPY",FACE,{"derivedFrom":makeQuery(id+"F3.opExtrude","CAP_FACE",FACE,{"disambiguationData":[OSD([sQuery(id+"F2.wireOp",EDGE,"E2.2.0.0"),sQuery(id+"F2.wireOp",EDGE,"E2.2.0.1"),sQuery(id+"F2.wireOp",EDGE,"E2.2.0.2"),sQuery(id+"F2.wireOp",EDGE,"E2.2.0.3")])],"isStart":false})}),makeQuery(id+"F5.opExtrude","SWEPT_FACE",FACE,{"disambiguationData":[OSD([sQuery(id+"F4.wireOp",EDGE,"E5.2.0.2")])]})]});
            var Q12;
            Q12=makeQuery(id+"F5.boolean.opBoolean","MERGE",FACE,{"derivedFrom":[makeQuery(id+"F3.boolean.opBoolean","COPY",FACE,{"derivedFrom":makeQuery(id+"F3.opExtrude","CAP_FACE",FACE,{"disambiguationData":[OSD([sQuery(id+"F2.wireOp",EDGE,"E3.0.3.0"),sQuery(id+"F2.wireOp",EDGE,"E3.3.3.0"),sQuery(id+"F2.wireOp",EDGE,"E3.6.3.0"),sQuery(id+"F2.wireOp",EDGE,"E3.9.3.0")])],"isStart":false})}),makeQuery(id+"F5.opExtrude","SWEPT_FACE",FACE,{"disambiguationData":[OSD([sQuery(id+"F4.wireOp",EDGE,"E5.3.0.2")])]})]});
            var Q13;
            Q13=makeQuery(id+"F5.boolean.opBoolean","MERGE",FACE,{"derivedFrom":[makeQuery(id+"F3.boolean.opBoolean","COPY",FACE,{"derivedFrom":makeQuery(id+"F3.opExtrude","CAP_FACE",FACE,{"disambiguationData":[OSD([sQuery(id+"F2.wireOp",EDGE,"E3.0.4.0"),sQuery(id+"F2.wireOp",EDGE,"E3.3.4.0"),sQuery(id+"F2.wireOp",EDGE,"E3.6.4.0"),sQuery(id+"F2.wireOp",EDGE,"E3.9.4.0")])],"isStart":false})}),makeQuery(id+"F5.opExtrude","SWEPT_FACE",FACE,{"disambiguationData":[OSD([sQuery(id+"F4.wireOp",EDGE,"E5.4.0.2")])]})]});
            var Q14;
            Q14=makeQuery(id+"F3.boolean.opBoolean","COPY",FACE,{"derivedFrom":makeQuery(id+"F3.opExtrude","SWEPT_FACE",FACE,{"disambiguationData":[OSD([sQuery(id+"F2.wireOp",EDGE,"E1.bottom")])]})});
            var Q15;
            Q15=makeQuery(id+"F3.boolean.opBoolean","COPY",FACE,{"derivedFrom":makeQuery(id+"F3.opExtrude","SWEPT_FACE",FACE,{"disambiguationData":[OSD([sQuery(id+"F2.wireOp",EDGE,"E2.1.0.1")])]})});
            var Q16;
            Q16=makeQuery(id+"F3.boolean.opBoolean","COPY",FACE,{"derivedFrom":makeQuery(id+"F3.opExtrude","SWEPT_FACE",FACE,{"disambiguationData":[OSD([sQuery(id+"F2.wireOp",EDGE,"E2.2.0.1")])]})});
            var Q17;
            Q17=makeQuery(id+"F3.boolean.opBoolean","COPY",FACE,{"derivedFrom":makeQuery(id+"F3.opExtrude","SWEPT_FACE",FACE,{"disambiguationData":[OSD([sQuery(id+"F2.wireOp",EDGE,"E3.3.3.0")])]})});
            var Q18;
            Q18=makeQuery(id+"F3.boolean.opBoolean","COPY",FACE,{"derivedFrom":makeQuery(id+"F3.opExtrude","SWEPT_FACE",FACE,{"disambiguationData":[OSD([sQuery(id+"F2.wireOp",EDGE,"E3.3.4.0")])]})});
            chamfer(context, id + "F11", {"entities" : qUnion([Q0, Q1, Q2, Q3, Q4, Q5, Q6, Q7, Q8, Q9, Q10, Q11, Q12, Q13, Q14, Q15, Q16, Q17, Q18]), "width" : 1 * mm, "tangentPropagation" : true});
        }
    });
